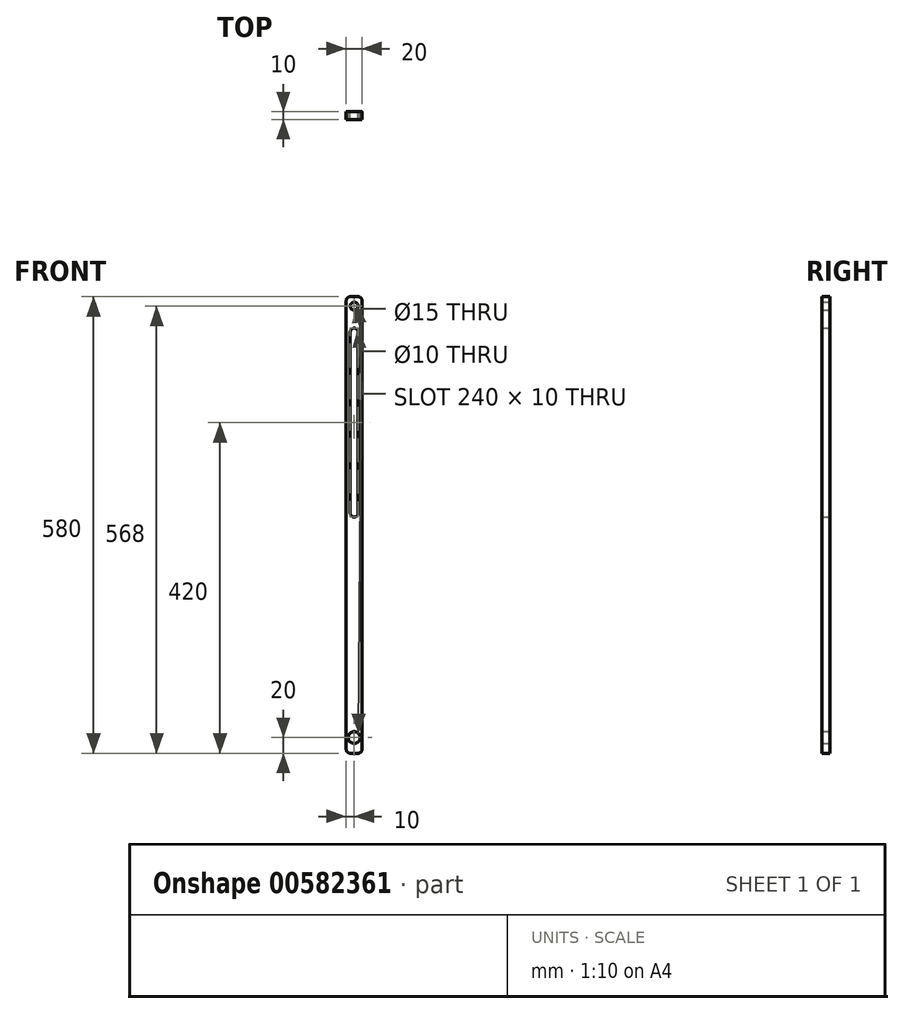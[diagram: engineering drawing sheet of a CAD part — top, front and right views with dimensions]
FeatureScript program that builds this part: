
annotation { "Feature Type Name" : "Feature", "Feature Type Description" : "" }
export const myFeature = defineFeature(function(context is Context, id is Id, definition is map)
    precondition{}
    {
        {
            var Q0;
            Q0=qCreatedBy(makeId("Front.planeOp"),FACE);
            var sketch = newSketch(context, id + "F0", { "sketchPlane" : qUnion([Q0])});
            skLineSegment(sketch, "E0.bottom", {"start": v(5, 290) * mm, "end": v(-5, 290) * mm});
            skLineSegment(sketch, "E0.top", {"start": v(5, -290) * mm, "end": v(-5, -290) * mm});
            skLineSegment(sketch, "E0.left", {"start": v(10, 285) * mm, "end": v(10, -285) * mm});
            skLineSegment(sketch, "E0.right", {"start": v(-10, 285) * mm, "end": v(-10, -285) * mm});
            skPoint(sketch, "E0.middle", {"position": v(0, 0) * mm});
            skPoint(sketch, "E1.visualSharp", {"position": v(-10, -290) * mm});
            skArc(sketch, "E1.filletArc", {"start": v(-10, -285) * mm, "mid": v(-8.54, -288.54) * mm, "end": v(-5, -290) * mm});
            skPoint(sketch, "E2.visualSharp", {"position": v(10, -290) * mm});
            skArc(sketch, "E2.filletArc", {"start": v(5, -290) * mm, "mid": v(8.54, -288.54) * mm, "end": v(10, -285) * mm});
            skPoint(sketch, "E3.visualSharp", {"position": v(-10, 290) * mm});
            skArc(sketch, "E3.filletArc", {"start": v(-5, 290) * mm, "mid": v(-8.54, 288.54) * mm, "end": v(-10, 285) * mm});
            skPoint(sketch, "E4.visualSharp", {"position": v(10, 290) * mm});
            skArc(sketch, "E4.filletArc", {"start": v(10, 285) * mm, "mid": v(8.54, 288.54) * mm, "end": v(5, 290) * mm});
            skCircle(sketch, "E5", {"center": v(0, -270) * mm, "radius": 7.5 * mm});
            skLineSegment(sketch, "E6.bottom", {"start": v(0, 10) * mm, "end": v(0, 10) * mm});
            skLineSegment(sketch, "E6.top", {"start": v(0, 250) * mm, "end": v(0, 250) * mm});
            skLineSegment(sketch, "E6.left", {"start": v(5, 15) * mm, "end": v(5, 245) * mm});
            skLineSegment(sketch, "E6.right", {"start": v(-5, 15) * mm, "end": v(-5, 245) * mm});
            skPoint(sketch, "E6.middle", {"position": v(0, 130) * mm});
            skPoint(sketch, "E7.visualSharp", {"position": v(-5, 250) * mm});
            skArc(sketch, "E7.filletArc", {"start": v(0, 250) * mm, "mid": v(-3.54, 248.54) * mm, "end": v(-5, 245) * mm});
            skPoint(sketch, "E8.visualSharp", {"position": v(5, 250) * mm});
            skArc(sketch, "E8.filletArc", {"start": v(5, 245) * mm, "mid": v(3.54, 248.54) * mm, "end": v(0, 250) * mm});
            skPoint(sketch, "E9.visualSharp", {"position": v(-5, 10) * mm});
            skArc(sketch, "E9.filletArc", {"start": v(-5, 15) * mm, "mid": v(-3.54, 11.46) * mm, "end": v(0, 10) * mm});
            skPoint(sketch, "E10.visualSharp", {"position": v(5, 10) * mm});
            skArc(sketch, "E10.filletArc", {"start": v(0, 10) * mm, "mid": v(3.54, 11.46) * mm, "end": v(5, 15) * mm});
            skCircle(sketch, "E11", {"center": v(0, 278) * mm, "radius": 5 * mm});
            skPoint(sketch, "E11.centerSnap0", {"position": v(0, 290) * mm});
            skSolve(sketch);
        }
        {
            var Q0;
            Q0 = qSketchRegion(id + "F0", true);
            extrude(context, id + "F1", {"entities" : qUnion([Q0]), "depth" : 10 * mm, "offsetDistance" : 25 * mm});
        }
    });
